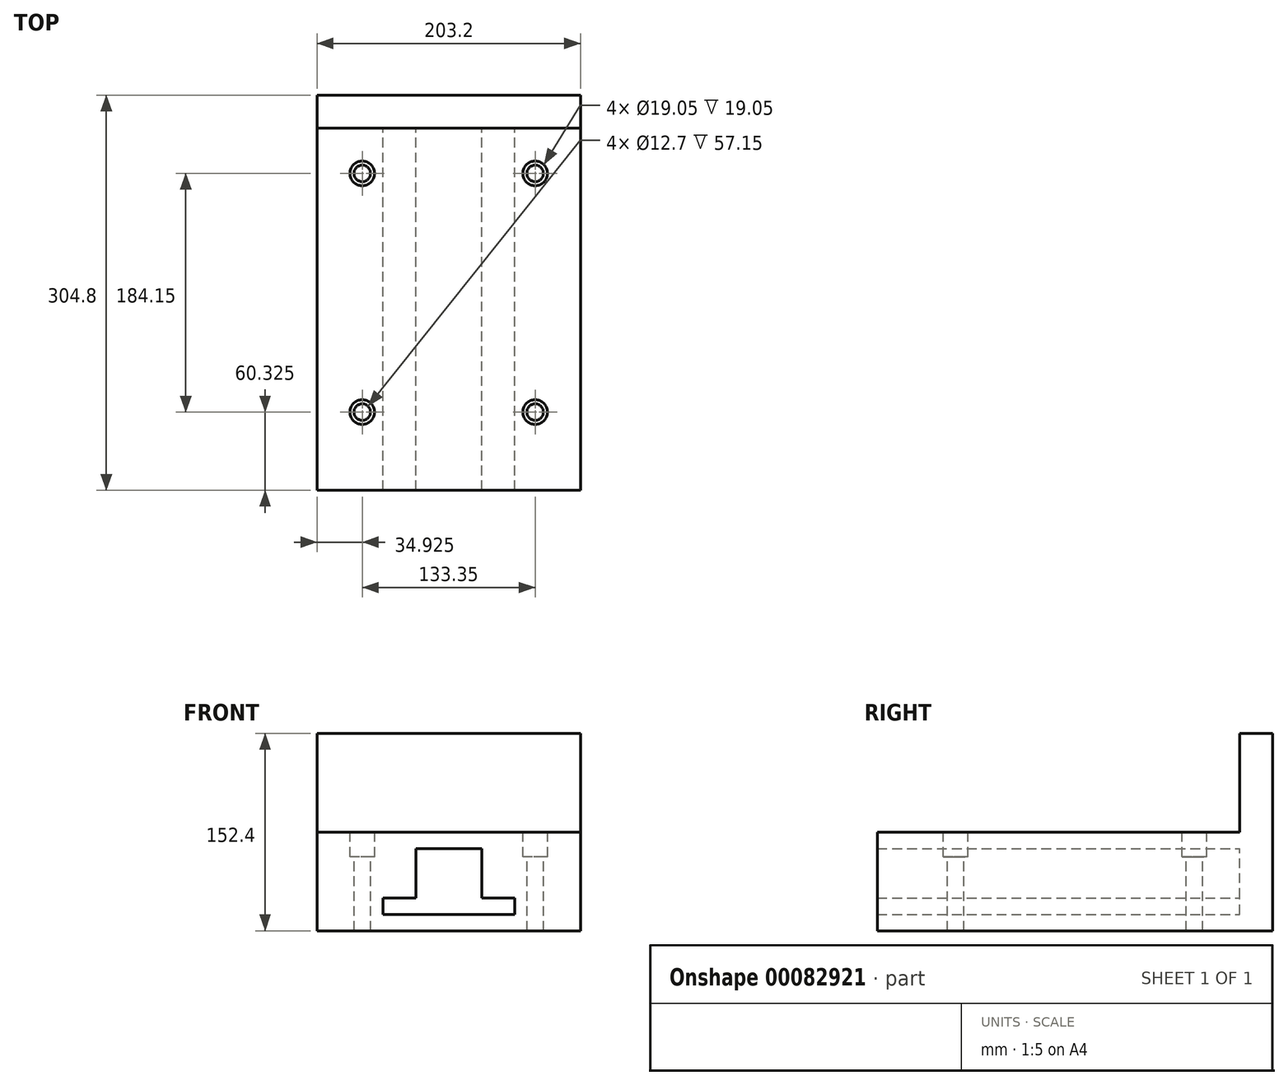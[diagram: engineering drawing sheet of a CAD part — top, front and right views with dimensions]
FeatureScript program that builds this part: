
annotation { "Feature Type Name" : "Feature", "Feature Type Description" : "" }
export const myFeature = defineFeature(function(context is Context, id is Id, definition is map)
    precondition{}
    {
        {
            var Q0;
            Q0=qCreatedBy(makeId("Front.planeOp"),FACE);
            var sketch = newSketch(context, id + "F0", { "sketchPlane" : qUnion([Q0])});
            skLineSegment(sketch, "E0.bottom", {"start": v(-101.6, 0) * mm, "end": v(101.6, 0) * mm});
            skLineSegment(sketch, "E0.top", {"start": v(-101.6, -76.2) * mm, "end": v(101.6, -76.2) * mm});
            skLineSegment(sketch, "E0.left", {"start": v(-101.6, 0) * mm, "end": v(-101.6, -76.2) * mm});
            skLineSegment(sketch, "E0.right", {"start": v(101.6, 0) * mm, "end": v(101.6, -76.2) * mm});
            skPoint(sketch, "E0.middle", {"position": v(0, -38.1) * mm});
            skLineSegment(sketch, "E1.bottom", {"start": v(-50.8, -50.8) * mm, "end": v(50.8, -50.8) * mm});
            skLineSegment(sketch, "E1.top", {"start": v(-50.8, -63.5) * mm, "end": v(50.8, -63.5) * mm});
            skLineSegment(sketch, "E1.left", {"start": v(-50.8, -50.8) * mm, "end": v(-50.8, -63.5) * mm});
            skLineSegment(sketch, "E1.right", {"start": v(50.8, -50.8) * mm, "end": v(50.8, -63.5) * mm});
            skPoint(sketch, "E1.middle", {"position": v(0, -57.15) * mm});
            skLineSegment(sketch, "E2", {"start": v(-25.4, -50.8) * mm, "end": v(-25.4, -12.7) * mm});
            skLineSegment(sketch, "E3", {"start": v(-25.4, -12.7) * mm, "end": v(25.4, -12.7) * mm});
            skLineSegment(sketch, "E4", {"start": v(25.4, -12.7) * mm, "end": v(25.4, -50.8) * mm});
            skCircle(sketch, "E5", {"center": v(0, -31.75) * mm, "radius": 6.35 * mm});
            skSolve(sketch);
        }
        {
            var Q0;
            Q0=makeQuery(id+"F0.imprint","IMPRINT",FACE,{"disambiguationData":[TD([[makeQuery(id+"F0.imprint","IMPRINT",EDGE,{"derivedFrom":sQuery(id+"F0.wireOp",EDGE,"E0.bottom")}),-1.0]])]});
            extrude(context, id + "F1", {"entities" : qUnion([Q0]), "depth" : 304.8 * mm});
        }
        {
            var Q0;
            Q0=qCreatedBy(makeId("Top.planeOp"),FACE);
            var sketch = newSketch(context, id + "F2", { "sketchPlane" : qUnion([Q0])});
            skLineSegment(sketch, "E6", {"start": v(-23.24, -12.7) * mm, "end": v(25.52, -12.7) * mm, "construction": true});
            skLineSegment(sketch, "E7.bottom", {"start": v(-101.6, -25.4) * mm, "end": v(101.6, -25.4) * mm});
            skLineSegment(sketch, "E7.top", {"start": v(-101.6, 0) * mm, "end": v(101.6, 0) * mm});
            skLineSegment(sketch, "E7.left", {"start": v(-101.6, -25.4) * mm, "end": v(-101.6, 0) * mm});
            skLineSegment(sketch, "E7.right", {"start": v(101.6, -25.4) * mm, "end": v(101.6, 0) * mm});
            skPoint(sketch, "E7.middle", {"position": v(0, -12.7) * mm});
            skPoint(sketch, "E7.middle.positionSnap0", {"position": v(1.14, -12.7) * mm});
            skPoint(sketch, "E7.centerSnap0", {"position": v(1.14, -12.7) * mm});
            skSolve(sketch);
        }
        {
            var Q0;
            Q0 = qSketchRegion(id + "F2", true);
            extrude(context, id + "F3", {"entities" : qUnion([Q0]), "operationType" : NewBodyOperationType.ADD, "endBound" : BoundingType.SYMMETRIC, "depth" : 152.4 * mm});
        }
        {
            var Q0;
            Q0=qCreatedBy(makeId("Top.planeOp"),FACE);
            var sketch = newSketch(context, id + "F4", { "sketchPlane" : qUnion([Q0])});
            skLineSegment(sketch, "E8", {"start": v(-98.49, -152.4) * mm, "end": v(98.49, -152.4) * mm, "construction": true});
            skLineSegment(sketch, "E9", {"start": v(0, 25.88) * mm, "end": v(0, -305.3) * mm, "construction": true});
            skCircle(sketch, "E10", {"center": v(-66.68, -60.33) * mm, "radius": 9.52 * mm});
            skCircle(sketch, "E11", {"center": v(-66.68, -60.33) * mm, "radius": 6.35 * mm});
            skCircle(sketch, "E12.MirrorC", {"center": v(66.68, -60.33) * mm, "radius": 9.52 * mm});
            skCircle(sketch, "E13.MirrorC", {"center": v(66.68, -60.33) * mm, "radius": 6.35 * mm});
            skLineSegment(sketch, "E14.MirrorCS", {"start": v(98.49, -152.4) * mm, "end": v(-98.49, -152.4) * mm, "construction": true});
            skCircle(sketch, "E15.MirrorC", {"center": v(66.68, -244.47) * mm, "radius": 6.35 * mm});
            skCircle(sketch, "E16.MirrorC", {"center": v(-66.68, -244.47) * mm, "radius": 6.35 * mm});
            skCircle(sketch, "E17.MirrorC", {"center": v(66.68, -244.47) * mm, "radius": 9.52 * mm});
            skCircle(sketch, "E18.MirrorC", {"center": v(-66.68, -244.47) * mm, "radius": 9.52 * mm});
            skSolve(sketch);
        }
        {
            var Q0;
            Q0 = qSketchRegion(id + "F4", true);
            extrude(context, id + "F5", {"entities" : qUnion([Q0]), "operationType" : NewBodyOperationType.REMOVE, "oppositeDirection" : true, "depth" : 19.05 * mm});
        }
        {
            var Q0;
            Q0=makeQuery(id+"F5.boolean.opBoolean","SPLIT",FACE,{"disambiguationData":[TD([makeQuery(id+"F5.opExtrude","SWEPT_FACE",FACE,{"disambiguationData":[OSD([sQuery(id+"F4.wireOp",EDGE,"E11")])]})])],"derivedFrom":makeQuery(id+"F1.opExtrude","SWEPT_FACE",FACE,{"disambiguationData":[OSD([sQuery(id+"F0.wireOp",EDGE,"E0.bottom")])]})});
            var Q1;
            Q1=makeQuery(id+"F5.boolean.opBoolean","SPLIT",FACE,{"disambiguationData":[TD([makeQuery(id+"F5.opExtrude","SWEPT_FACE",FACE,{"disambiguationData":[OSD([sQuery(id+"F4.wireOp",EDGE,"E13.MirrorC")])]})])],"derivedFrom":makeQuery(id+"F1.opExtrude","SWEPT_FACE",FACE,{"disambiguationData":[OSD([sQuery(id+"F0.wireOp",EDGE,"E0.bottom")])]})});
            var Q2;
            Q2=makeQuery(id+"F5.boolean.opBoolean","SPLIT",FACE,{"disambiguationData":[TD([makeQuery(id+"F5.opExtrude","SWEPT_FACE",FACE,{"disambiguationData":[OSD([sQuery(id+"F4.wireOp",EDGE,"E16.MirrorC")])]})])],"derivedFrom":makeQuery(id+"F1.opExtrude","SWEPT_FACE",FACE,{"disambiguationData":[OSD([sQuery(id+"F0.wireOp",EDGE,"E0.bottom")])]})});
            var Q3;
            Q3=makeQuery(id+"F5.boolean.opBoolean","SPLIT",FACE,{"disambiguationData":[TD([makeQuery(id+"F5.opExtrude","SWEPT_FACE",FACE,{"disambiguationData":[OSD([sQuery(id+"F4.wireOp",EDGE,"E15.MirrorC")])]})])],"derivedFrom":makeQuery(id+"F1.opExtrude","SWEPT_FACE",FACE,{"disambiguationData":[OSD([sQuery(id+"F0.wireOp",EDGE,"E0.bottom")])]})});
            extrude(context, id + "F6", {"entities" : qUnion([Q0, Q1, Q2, Q3]), "operationType" : NewBodyOperationType.REMOVE, "endBound" : BoundingType.THROUGH_ALL, "oppositeDirection" : true, "depth" : 25.4 * mm});
        }
    });
